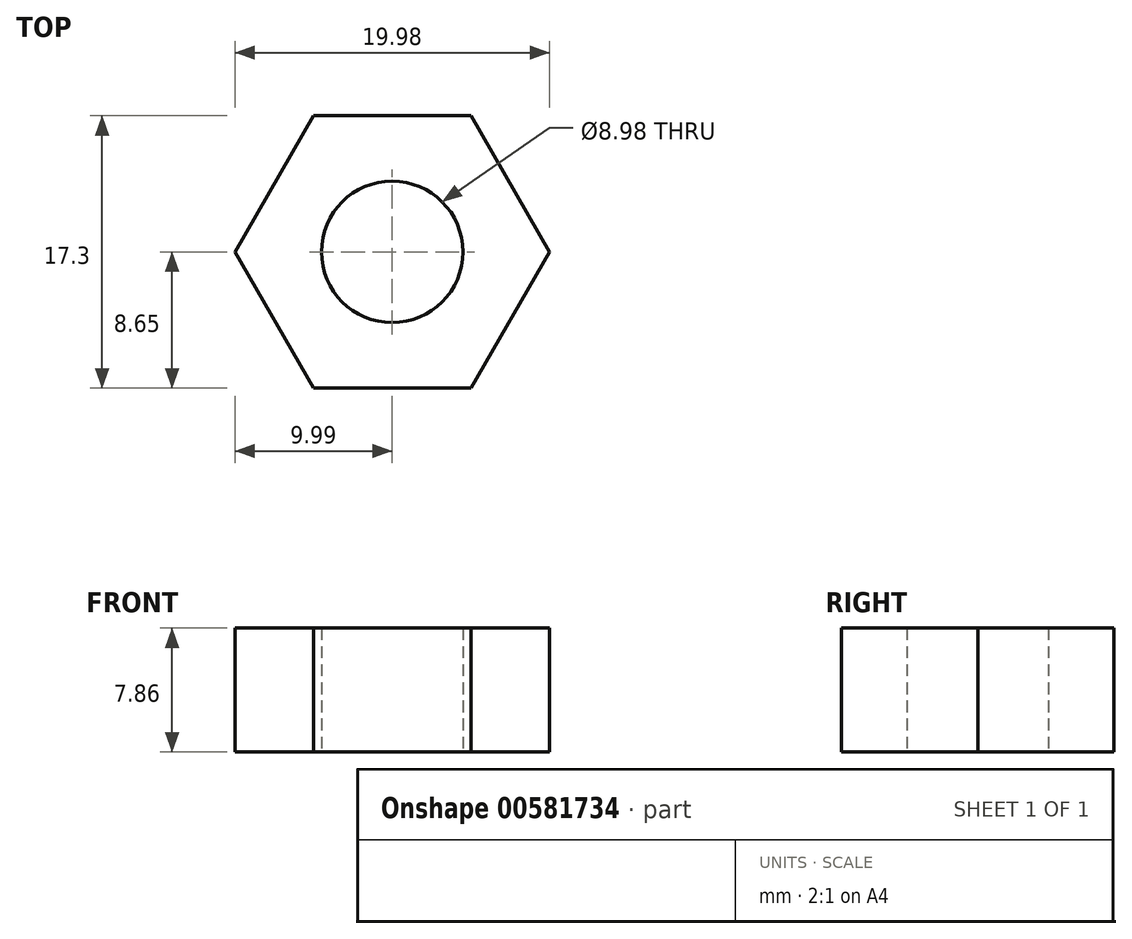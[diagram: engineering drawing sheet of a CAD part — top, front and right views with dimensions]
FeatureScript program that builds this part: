
annotation { "Feature Type Name" : "Feature", "Feature Type Description" : "" }
export const myFeature = defineFeature(function(context is Context, id is Id, definition is map)
    precondition{}
    {
        {
            var Q0;
            Q0=qCreatedBy(makeId("Top.planeOp"),FACE);
            var sketch = newSketch(context, id + "F0", { "sketchPlane" : qUnion([Q0])});
            skCircle(sketch, "E0.cCircle", {"center": v(0, 0) * mm, "radius": 8.65 * mm, "construction": true});
            skLineSegment(sketch, "E0.0", {"start": v(-5, 8.65) * mm, "end": v(5, 8.65) * mm});
            skLineSegment(sketch, "E0.1", {"start": v(5, 8.65) * mm, "end": v(9.99, 0) * mm});
            skLineSegment(sketch, "E0.2", {"start": v(9.99, 0) * mm, "end": v(5, -8.65) * mm});
            skLineSegment(sketch, "E0.3", {"start": v(5, -8.65) * mm, "end": v(-5, -8.65) * mm});
            skLineSegment(sketch, "E0.4", {"start": v(-5, -8.65) * mm, "end": v(-9.99, 0) * mm});
            skLineSegment(sketch, "E0.5", {"start": v(-9.99, 0) * mm, "end": v(-5, 8.65) * mm});
            skPoint(sketch, "E0.0.midPoint", {"position": v(0, 8.65) * mm});
            skCircle(sketch, "E1", {"center": v(0, 0) * mm, "radius": 4.49 * mm});
            skLineSegment(sketch, "E2", {"start": v(-7.4, -4.5) * mm, "end": v(7.4, -4.49) * mm, "construction": true});
            skSolve(sketch);
        }
        {
            var Q0;
            Q0=makeQuery(id+"F0.imprint","IMPRINT",FACE,{"disambiguationData":[TD([[makeQuery(id+"F0.imprint","IMPRINT",EDGE,{"derivedFrom":sQuery(id+"F0.wireOp",EDGE,"E0.0")}),-1.0]])]});
            extrude(context, id + "F1", {"entities" : qUnion([Q0]), "depth" : 7.86 * mm, "offsetDistance" : 25 * mm});
        }
    });
